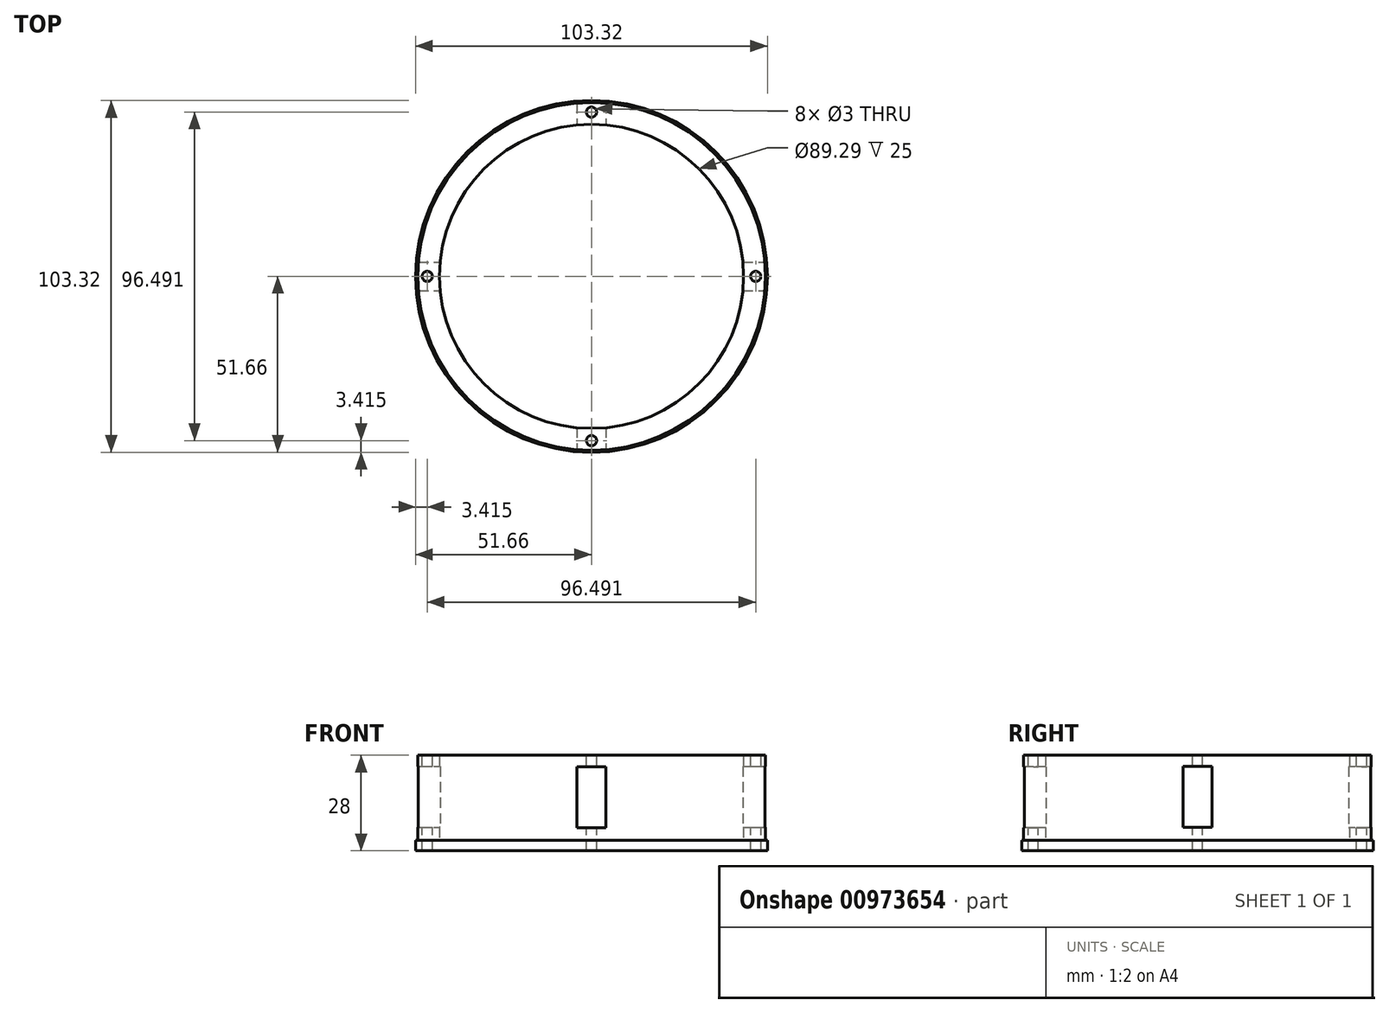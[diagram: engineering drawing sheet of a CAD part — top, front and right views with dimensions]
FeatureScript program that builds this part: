
annotation { "Feature Type Name" : "Feature", "Feature Type Description" : "" }
export const myFeature = defineFeature(function(context is Context, id is Id, definition is map)
    precondition{}
    {
        {
            var Q0;
            Q0=qCreatedBy(makeId("Top.planeOp"),FACE);
            var sketch = newSketch(context, id + "F0", { "sketchPlane" : qUnion([Q0])});
            skCircle(sketch, "E0", {"center": v(0, 0) * mm, "radius": 51.06 * mm});
            skCircle(sketch, "E1", {"center": v(0, 0) * mm, "radius": 44.65 * mm});
            skSolve(sketch);
        }
        {
            var Q0;
            Q0=makeQuery(id+"F0.imprint","IMPRINT",FACE,{"disambiguationData":[TD([[makeQuery(id+"F0.imprint","IMPRINT",EDGE,{"derivedFrom":sQuery(id+"F0.wireOp",EDGE,"E0")}),1.0]])]});
            extrude(context, id + "F1", {"entities" : qUnion([Q0]), "depth" : 25 * mm, "offsetDistance" : 25 * mm});
        }
        {
            var Q0;
            Q0=makeQuery(id+"F1.opExtrude","CAP_FACE",FACE,{"disambiguationData":[OSD([sQuery(id+"F0.wireOp",EDGE,"E0"),sQuery(id+"F0.wireOp",EDGE,"E1")])],"isStart":true});
            var sketch = newSketch(context, id + "F2", { "sketchPlane" : qUnion([Q0])});
            skCircle(sketch, "E2", {"center": v(0, 0) * mm, "radius": 51.66 * mm});
            skSolve(sketch);
        }
        {
            var Q0;
            Q0 = qSketchRegion(id + "F2", true);
            extrude(context, id + "F3", {"entities" : qUnion([Q0]), "operationType" : NewBodyOperationType.ADD, "depth" : 3 * mm, "offsetDistance" : 25 * mm});
        }
        {
            var Q0;
            Q0=qCreatedBy(makeId("Front.planeOp"),FACE);
            var sketch = newSketch(context, id + "F4", { "sketchPlane" : qUnion([Q0])});
            skLineSegment(sketch, "E3.bottom", {"start": v(-4.24, 21.68) * mm, "end": v(4.24, 21.68) * mm});
            skLineSegment(sketch, "E3.top", {"start": v(-4.24, 3.76) * mm, "end": v(4.24, 3.76) * mm});
            skLineSegment(sketch, "E3.left", {"start": v(-4.24, 21.68) * mm, "end": v(-4.24, 3.76) * mm});
            skLineSegment(sketch, "E3.right", {"start": v(4.24, 21.68) * mm, "end": v(4.24, 3.76) * mm});
            skPoint(sketch, "E3.middle", {"position": v(0, 12.72) * mm});
            skSolve(sketch);
        }
        {
            var Q0;
            Q0=makeQuery(id+"F4.imprint","IMPRINT",FACE,{"disambiguationData":[TD([[makeQuery(id+"F4.imprint","IMPRINT",EDGE,{"derivedFrom":sQuery(id+"F4.wireOp",EDGE,"E3.bottom")}),-1.0]])]});
            extrude(context, id + "F5", {"entities" : qUnion([Q0]), "operationType" : NewBodyOperationType.REMOVE, "oppositeDirection" : true, "depth" : 174.4 * mm, "offsetDistance" : 25 * mm, "symmetric" : true});
        }
        {
            var Q0;
            Q0=qCreatedBy(makeId("Right.planeOp"),FACE);
            var sketch = newSketch(context, id + "F6", { "sketchPlane" : qUnion([Q0])});
            skLineSegment(sketch, "E4.bottom", {"start": v(-4.24, 21.77) * mm, "end": v(4.24, 21.77) * mm});
            skLineSegment(sketch, "E4.top", {"start": v(-4.24, 3.85) * mm, "end": v(4.24, 3.85) * mm});
            skLineSegment(sketch, "E4.left", {"start": v(-4.24, 21.77) * mm, "end": v(-4.24, 3.85) * mm});
            skLineSegment(sketch, "E4.right", {"start": v(4.24, 21.77) * mm, "end": v(4.24, 3.85) * mm});
            skPoint(sketch, "E4.middle", {"position": v(0, 12.8) * mm});
            skSolve(sketch);
        }
        {
            var Q0;
            Q0=makeQuery(id+"F6.imprint","IMPRINT",FACE,{"disambiguationData":[TD([[makeQuery(id+"F6.imprint","IMPRINT",EDGE,{"derivedFrom":sQuery(id+"F6.wireOp",EDGE,"E4.bottom")}),-1.0]])]});
            extrude(context, id + "F7", {"entities" : qUnion([Q0]), "operationType" : NewBodyOperationType.REMOVE, "oppositeDirection" : true, "depth" : 123.8 * mm, "offsetDistance" : 25 * mm, "symmetric" : true});
        }
        {
            var Q0;
            Q0=makeQuery(id+"F1.opExtrude","CAP_FACE",FACE,{"disambiguationData":[OSD([sQuery(id+"F0.wireOp",EDGE,"E0"),sQuery(id+"F0.wireOp",EDGE,"E1")])],"isStart":false});
            var sketch = newSketch(context, id + "F8", { "sketchPlane" : qUnion([Q0])});
            skCircle(sketch, "E5", {"center": v(0, 48.25) * mm, "radius": 1.5 * mm});
            skCircle(sketch, "E6.1.0", {"center": v(-48.25, 0) * mm, "radius": 1.5 * mm});
            skCircle(sketch, "E6.2.0", {"center": v(0, -48.25) * mm, "radius": 1.5 * mm});
            skPoint(sketch, "E6.center", {"position": v(0, 0) * mm});
            skCircle(sketch, "E7.1.3.0", {"center": v(48.25, 0) * mm, "radius": 1.5 * mm});
            skSolve(sketch);
        }
        {
            var Q0;
            Q0=makeQuery(id+"F8.imprint","IMPRINT",FACE,{"disambiguationData":[TD([[makeQuery(id+"F8.imprint","IMPRINT",EDGE,{"derivedFrom":sQuery(id+"F8.wireOp",EDGE,"E5")}),1.0]])]});
            var Q1;
            Q1=makeQuery(id+"F8.imprint","IMPRINT",FACE,{"disambiguationData":[TD([[makeQuery(id+"F8.imprint","IMPRINT",EDGE,{"derivedFrom":sQuery(id+"F8.wireOp",EDGE,"E6.2.0")}),1.0]])]});
            var Q2;
            Q2=makeQuery(id+"F8.imprint","IMPRINT",FACE,{"disambiguationData":[TD([[makeQuery(id+"F8.imprint","IMPRINT",EDGE,{"derivedFrom":sQuery(id+"F8.wireOp",EDGE,"E6.1.0")}),1.0]])]});
            var Q3;
            Q3=makeQuery(id+"F8.imprint","IMPRINT",FACE,{"disambiguationData":[TD([[makeQuery(id+"F8.imprint","IMPRINT",EDGE,{"derivedFrom":sQuery(id+"F8.wireOp",EDGE,"E7.1.3.0")}),1.0]])]});
            extrude(context, id + "F9", {"entities" : qUnion([Q0, Q1, Q2, Q3]), "operationType" : NewBodyOperationType.REMOVE, "endBound" : BoundingType.THROUGH_ALL, "oppositeDirection" : true, "depth" : 25 * mm, "offsetDistance" : 25 * mm});
        }
    });
